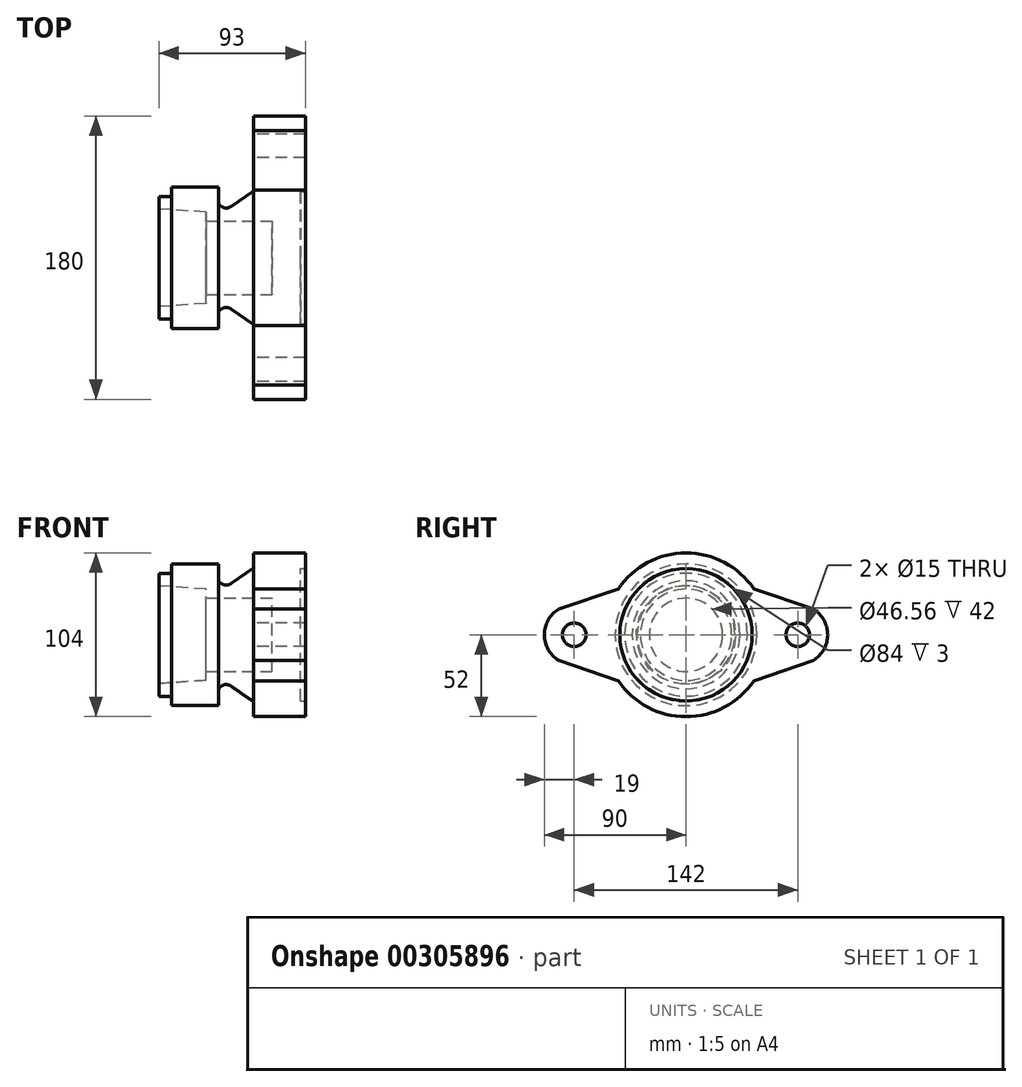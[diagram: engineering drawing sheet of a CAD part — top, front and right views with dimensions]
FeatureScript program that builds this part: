
annotation { "Feature Type Name" : "Feature", "Feature Type Description" : "" }
export const myFeature = defineFeature(function(context is Context, id is Id, definition is map)
    precondition{}
    {
        {
            var Q0;
            Q0=qCreatedBy(makeId("Front.planeOp"),FACE);
            var sketch = newSketch(context, id + "F0", { "sketchPlane" : qUnion([Q0])});
            skLineSegment(sketch, "E0", {"start": v(0, 31) * mm, "end": v(0, 39) * mm});
            skLineSegment(sketch, "E1", {"start": v(0, 39) * mm, "end": v(8, 39) * mm});
            skLineSegment(sketch, "E2", {"start": v(8, 39) * mm, "end": v(8, 45) * mm});
            skLineSegment(sketch, "E3", {"start": v(8, 45) * mm, "end": v(38, 45) * mm});
            skLineSegment(sketch, "E4", {"start": v(38, 45) * mm, "end": v(38, 34.26) * mm});
            skLineSegment(sketch, "E5", {"start": v(45.82, 32.57) * mm, "end": v(60, 42.5) * mm});
            skLineSegment(sketch, "E6", {"start": v(60, 42.5) * mm, "end": v(60, 52) * mm});
            skLineSegment(sketch, "E7", {"start": v(60, 52) * mm, "end": v(93, 52) * mm});
            skLineSegment(sketch, "E8", {"start": v(93, 52) * mm, "end": v(93, 42) * mm});
            skLineSegment(sketch, "E9", {"start": v(93, 42) * mm, "end": v(90, 42) * mm});
            skLineSegment(sketch, "E10", {"start": v(90, 42) * mm, "end": v(90, 0) * mm});
            skLineSegment(sketch, "E11", {"start": v(90, 0) * mm, "end": v(72, 0) * mm});
            skLineSegment(sketch, "E12", {"start": v(72, 0) * mm, "end": v(72, 23.28) * mm});
            skLineSegment(sketch, "E13", {"start": v(72, 23.28) * mm, "end": v(30, 23.28) * mm});
            skLineSegment(sketch, "E14", {"start": v(30, 23.28) * mm, "end": v(30, 29) * mm});
            skLineSegment(sketch, "E15", {"start": v(30, 29) * mm, "end": v(0, 31) * mm});
            skArc(sketch, "E16", {"start": v(38, 34.26) * mm, "mid": v(41.6, 31.72) * mm, "end": v(45.9, 32.63) * mm});
            skSolve(sketch);
        }
        {
            var Q0;
            Q0=makeQuery(id+"F0.imprint","IMPRINT",FACE,{"disambiguationData":[TD([[makeQuery(id+"F0.imprint","IMPRINT",EDGE,{"derivedFrom":sQuery(id+"F0.wireOp",EDGE,"E0")}),-1.0]])]});
            var Q1;
            Q1=sQuery(id+"F0.wireOp",EDGE,"E11");
            revolve(context, id + "F1", {"entities" : qUnion([Q0]), "axis" : qUnion([Q1]), "revolveType" : RevolveType.FULL});
        }
        {
            var Q0;
            Q0=makeQuery(id+"F1.opRevolve","SWEPT_FACE",FACE,{"disambiguationData":[OSD([sQuery(id+"F0.wireOp",EDGE,"E10")])]});
            var sketch = newSketch(context, id + "F2", { "sketchPlane" : qUnion([Q0])});
            skArc(sketch, "E17", {"start": v(-80.82, 16.27) * mm, "mid": v(-90, 0) * mm, "end": v(-80.82, -16.27) * mm});
            skCircle(sketch, "E18", {"center": v(-71, 0) * mm, "radius": 7.5 * mm});
            skCircle(sketch, "E19", {"center": v(71, 0) * mm, "radius": 7.5 * mm});
            skArc(sketch, "E20", {"start": v(80.82, -16.27) * mm, "mid": v(90, 0) * mm, "end": v(80.82, 16.27) * mm});
            skLineSegment(sketch, "E21", {"start": v(-7.82, 41.27) * mm, "end": v(-80.82, 16.27) * mm});
            skLineSegment(sketch, "E22", {"start": v(-7.82, -41.27) * mm, "end": v(-80.82, -16.27) * mm});
            skLineSegment(sketch, "E23", {"start": v(7.82, 41.27) * mm, "end": v(80.82, 16.27) * mm});
            skLineSegment(sketch, "E24", {"start": v(7.82, -41.27) * mm, "end": v(80.82, -16.27) * mm});
            skSolve(sketch);
        }
        {
            var Q0;
            {var subQ1=sQuery(id+"F2.wireOp",EDGE,"E17");Q0=makeQuery(id+"F2.imprint","IMPRINT",FACE,{"disambiguationData":[TD([[makeQuery(id+"F2.imprint","IMPRINT",EDGE,{"derivedFrom":subQ1}),1.0]])]});}
            var Q1;
            Q1=makeQuery(id+"F2.imprint","IMPRINT",FACE,{"disambiguationData":[TD([[makeQuery(id+"F2.imprint","IMPRINT",EDGE,{"derivedFrom":sQuery(id+"F2.wireOp",EDGE,"E19")}),-1.0]])]});
            var Q2;
            Q2 = qSketchRegion(id + "F2", true);
            extrude(context, id + "F3", {"entities" : qUnion([Q0, Q1, Q2]), "operationType" : NewBodyOperationType.ADD, "oppositeDirection" : true, "depth" : 30 * mm});
        }
        {
            var Q0;
            Q0=makeQuery(id+"F3.opExtrude","CAP_FACE",FACE,{"disambiguationData":[OSD([sQuery(id+"F0.wireOp",EDGE,"E9"),sQuery(id+"F0.wireOp",EDGE,"E10"),sQuery(id+"F2.wireOp",EDGE,"E20"),sQuery(id+"F2.wireOp",EDGE,"E23"),sQuery(id+"F2.wireOp",EDGE,"E24")])],"isStart":true});
            var Q1;
            Q1=makeQuery(id+"F3.opExtrude","CAP_FACE",FACE,{"disambiguationData":[OSD([sQuery(id+"F0.wireOp",EDGE,"E9"),sQuery(id+"F0.wireOp",EDGE,"E10"),sQuery(id+"F2.wireOp",EDGE,"E17"),sQuery(id+"F2.wireOp",EDGE,"E21"),sQuery(id+"F2.wireOp",EDGE,"E22")])],"isStart":true});
            extrude(context, id + "F4", {"entities" : qUnion([Q0, Q1]), "operationType" : NewBodyOperationType.ADD, "depth" : 3 * mm});
        }
        {
            var Q0;
            {var subQ0=sQuery(id+"F0.wireOp",EDGE,"E10");var subQ1=sQuery(id+"F0.wireOp",EDGE,"E9");Q0=makeQuery(id+"F3.boolean.opBoolean","MERGE",FACE,{"derivedFrom":[makeQuery(id+"F1.opRevolve","SWEPT_FACE",FACE,{"disambiguationData":[OSD([sQuery(id+"F0.wireOp",EDGE,"E6")])]}),makeQuery(id+"F3.opExtrude","CAP_FACE",FACE,{"disambiguationData":[OSD([subQ1,subQ0,sQuery(id+"F2.wireOp",EDGE,"E17"),sQuery(id+"F2.wireOp",EDGE,"E21"),sQuery(id+"F2.wireOp",EDGE,"E22")])],"isStart":false}),makeQuery(id+"F3.opExtrude","CAP_FACE",FACE,{"disambiguationData":[OSD([subQ1,subQ0,sQuery(id+"F2.wireOp",EDGE,"E20"),sQuery(id+"F2.wireOp",EDGE,"E23"),sQuery(id+"F2.wireOp",EDGE,"E24")])],"isStart":false})]});}
            var sketch = newSketch(context, id + "F5", { "sketchPlane" : qUnion([Q0])});
            skCircle(sketch, "E25", {"center": v(-71, 0) * mm, "radius": 7.5 * mm});
            skCircle(sketch, "E26", {"center": v(71, 0) * mm, "radius": 7.5 * mm});
            skSolve(sketch);
        }
        {
            var Q0;
            Q0=makeQuery(id+"F5.imprint","IMPRINT",FACE,{"disambiguationData":[TD([[makeQuery(id+"F5.imprint","IMPRINT",EDGE,{"derivedFrom":sQuery(id+"F5.wireOp",EDGE,"E25")}),1.0]])]});
            extrude(context, id + "F6", {"entities" : qUnion([Q0]), "operationType" : NewBodyOperationType.REMOVE, "oppositeDirection" : true, "depth" : 33 * mm});
        }
        {
            var Q0;
            Q0=makeQuery(id+"F5.imprint","IMPRINT",FACE,{"disambiguationData":[TD([[makeQuery(id+"F5.imprint","IMPRINT",EDGE,{"derivedFrom":sQuery(id+"F5.wireOp",EDGE,"E26")}),1.0]])]});
            var sketch = newSketch(context, id + "F7", { "sketchPlane" : qUnion([Q0])});
            skSolve(sketch);
        }
        {
            var Q0;
            Q0=makeQuery(id+"F7.imprint","IMPRINT",FACE,{"disambiguationData":[TD([[makeQuery(id+"F7.imprint","IMPRINT",EDGE,{"derivedFrom":makeQuery(id+"F5.imprint","IMPRINT",EDGE,{"derivedFrom":sQuery(id+"F5.wireOp",EDGE,"E26")})}),1.0]])]});
            extrude(context, id + "F8", {"entities" : qUnion([Q0]), "operationType" : NewBodyOperationType.REMOVE, "oppositeDirection" : true, "depth" : 33 * mm});
        }
    });
